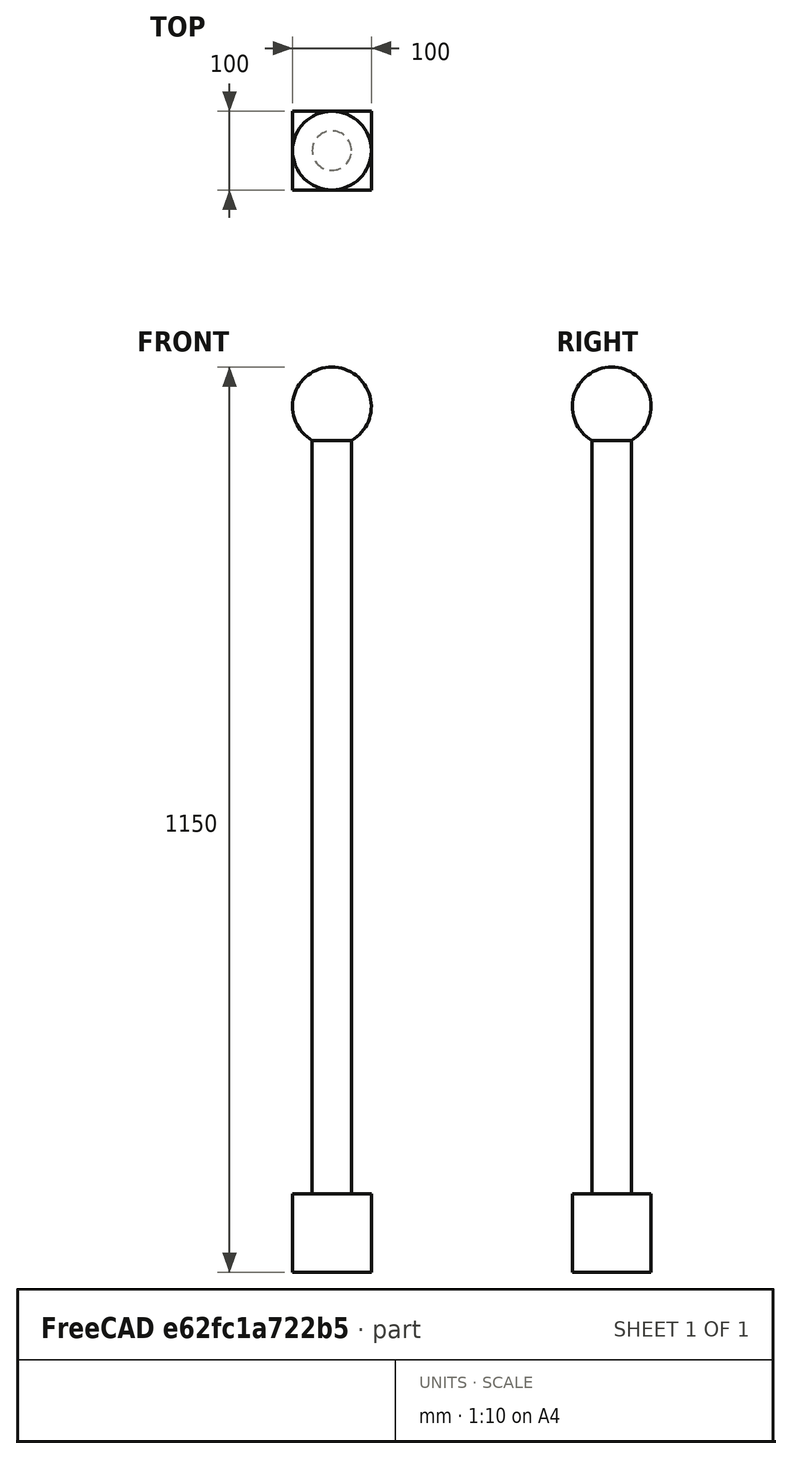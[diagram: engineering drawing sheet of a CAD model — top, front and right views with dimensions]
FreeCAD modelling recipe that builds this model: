
FCSTD DOCUMENT  (FreeCAD 1.0R39319 (Git))
Label: new shape1
License: All rights reserved
LicenseURL: https://en.wikipedia.org/wiki/All_rights_reserved
objects: Part::Box×1, Part::Cylinder×1, Part::Sphere×1, Part::MultiFuse×1
note: 4 computed .brp shape members not serialized (recipe doc carries the construction recipe); baked Part::Feature solids carry a one-line shape summary decoded from their .brp

FEATURE [Part::Box] cube
  AttacherType = Attacher::AttachEngine3D
  Height = 100
  Length = 100
  Placement = pos=(-50,-50,0) rot=(0,0,1;0rad)
  Width = 100
FEATURE [Part::Cylinder] cylinder
  Angle = 360
  AttacherType = Attacher::AttachEngine3D
  FirstAngle = 0
  Height = 1000
  Placement = pos=(0,0,100) rot=(0,0,1;0rad)
  Radius = 25
  SecondAngle = 0
FEATURE [Part::Sphere] sphere
  Angle1 = -90
  Angle2 = 90
  Angle3 = 360
  AttacherType = Attacher::AttachEngine3D
  Placement = pos=(0,0,1100) rot=(0,0,1;0rad)
  Radius = 50
FEATURE [Part::MultiFuse] union
  Shapes = -> [cube,cylinder,sphere]
